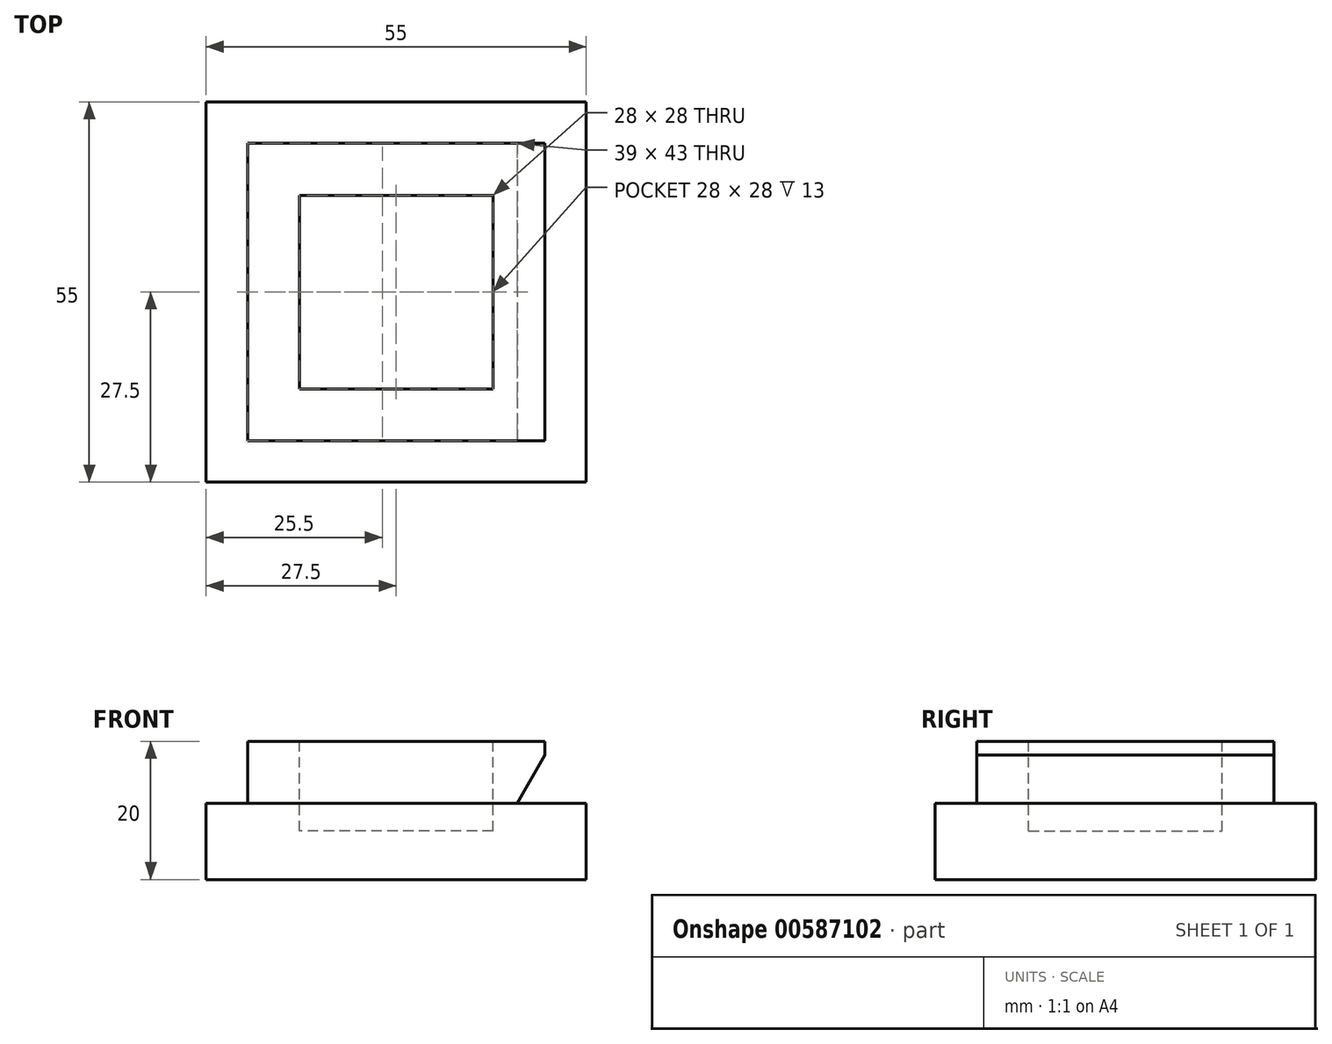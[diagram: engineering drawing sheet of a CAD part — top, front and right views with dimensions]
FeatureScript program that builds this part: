
annotation { "Feature Type Name" : "Feature", "Feature Type Description" : "" }
export const myFeature = defineFeature(function(context is Context, id is Id, definition is map)
    precondition{}
    {
        {
            var Q0;
            Q0=qCreatedBy(makeId("Top.planeOp"),FACE);
            var sketch = newSketch(context, id + "F0", { "sketchPlane" : qUnion([Q0])});
            skLineSegment(sketch, "E0.bottom", {"start": v(-27.5, 27.5) * mm, "end": v(27.5, 27.5) * mm});
            skLineSegment(sketch, "E0.top", {"start": v(-27.5, -27.5) * mm, "end": v(27.5, -27.5) * mm});
            skLineSegment(sketch, "E0.left", {"start": v(-27.5, 27.5) * mm, "end": v(-27.5, -27.5) * mm});
            skLineSegment(sketch, "E0.right", {"start": v(27.5, 27.5) * mm, "end": v(27.5, -27.5) * mm});
            skSolve(sketch);
        }
        {
            var Q0;
            Q0 = qSketchRegion(id + "F0", true);
            extrude(context, id + "F1", {"entities" : qUnion([Q0]), "depth" : 20 * mm, "offsetDistance" : 25 * mm});
        }
        {
            var Q0;
            Q0=qCreatedBy(makeId("Top.planeOp"),FACE);
            cPlane(context, id + "F2", {"entities" : qUnion([Q0]), "cplaneType" : CPlaneType.OFFSET, "offset" : 7 * mm, "width" : 150 * mm, "height" : 150 * mm});
        }
        {
            var Q0;
            Q0=makeQuery(id+"F1.opExtrude","CAP_FACE",FACE,{"disambiguationData":[OSD([sQuery(id+"F0.wireOp",EDGE,"E0.bottom"),sQuery(id+"F0.wireOp",EDGE,"E0.top"),sQuery(id+"F0.wireOp",EDGE,"E0.left"),sQuery(id+"F0.wireOp",EDGE,"E0.right")])],"isStart":false});
            var sketch = newSketch(context, id + "F3", { "sketchPlane" : qUnion([Q0])});
            skLineSegment(sketch, "E1.bottom", {"start": v(-14, 14) * mm, "end": v(14, 14) * mm});
            skLineSegment(sketch, "E1.top", {"start": v(-14, -14) * mm, "end": v(14, -14) * mm});
            skLineSegment(sketch, "E1.left", {"start": v(-14, 14) * mm, "end": v(-14, -14) * mm});
            skLineSegment(sketch, "E1.right", {"start": v(14, 14) * mm, "end": v(14, -14) * mm});
            skSolve(sketch);
        }
        {
            var Q0;
            Q0 = qSketchRegion(id + "F3", true);
            var Q1;
            Q1=qCreatedBy(id+"F2.planeOp",FACE);
            extrude(context, id + "F4", {"entities" : qUnion([Q0]), "operationType" : NewBodyOperationType.REMOVE, "endBound" : BoundingType.UP_TO_SURFACE, "oppositeDirection" : true, "depth" : 12 * mm, "endBoundEntityFace" : qUnion([Q1]), "offsetDistance" : 25 * mm});
        }
        {
            var Q0;
            Q0=makeQuery(id+"F1.opExtrude","CAP_FACE",FACE,{"disambiguationData":[OSD([sQuery(id+"F0.wireOp",EDGE,"E0.bottom"),sQuery(id+"F0.wireOp",EDGE,"E0.top"),sQuery(id+"F0.wireOp",EDGE,"E0.left"),sQuery(id+"F0.wireOp",EDGE,"E0.right")])],"isStart":false});
            var sketch = newSketch(context, id + "F5", { "sketchPlane" : qUnion([Q0])});
            skLineSegment(sketch, "E2.bottom", {"start": v(-21.5, 21.5) * mm, "end": v(21.5, 21.5) * mm});
            skLineSegment(sketch, "E2.top", {"start": v(-21.5, -21.5) * mm, "end": v(21.5, -21.5) * mm});
            skLineSegment(sketch, "E2.left", {"start": v(-21.5, 21.5) * mm, "end": v(-21.5, -21.5) * mm});
            skLineSegment(sketch, "E2.right", {"start": v(21.5, 21.5) * mm, "end": v(21.5, -21.5) * mm});
            skLineSegment(sketch, "E3.bottom", {"start": v(-27.5, 27.5) * mm, "end": v(27.5, 27.5) * mm});
            skLineSegment(sketch, "E3.top", {"start": v(-27.5, -27.5) * mm, "end": v(27.5, -27.5) * mm});
            skLineSegment(sketch, "E3.left", {"start": v(-27.5, 27.5) * mm, "end": v(-27.5, -27.5) * mm});
            skLineSegment(sketch, "E3.right", {"start": v(27.5, 27.5) * mm, "end": v(27.5, -27.5) * mm});
            skSolve(sketch);
        }
        {
            var Q0;
            Q0 = qSketchRegion(id + "F5", true);
            extrude(context, id + "F6", {"entities" : qUnion([Q0]), "operationType" : NewBodyOperationType.REMOVE, "oppositeDirection" : true, "depth" : 9 * mm, "offsetDistance" : 25 * mm});
        }
        {
            var Q0;
            Q0=qCreatedBy(makeId("Front.planeOp"),FACE);
            var sketch = newSketch(context, id + "F7", { "sketchPlane" : qUnion([Q0])});
            skLineSegment(sketch, "E4", {"start": v(21.5, 18) * mm, "end": v(17.5, 11) * mm});
            skLineSegment(sketch, "E5", {"start": v(17.5, 11) * mm, "end": v(21.5, 11) * mm});
            skLineSegment(sketch, "E6", {"start": v(21.5, 11) * mm, "end": v(21.5, 18) * mm});
            skSolve(sketch);
        }
        {
            var Q0;
            Q0 = qSketchRegion(id + "F7", true);
            extrude(context, id + "F8", {"entities" : qUnion([Q0]), "operationType" : NewBodyOperationType.REMOVE, "endBound" : BoundingType.SYMMETRIC, "oppositeDirection" : true, "depth" : 45 * mm, "offsetDistance" : 25 * mm});
        }
    });
